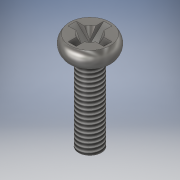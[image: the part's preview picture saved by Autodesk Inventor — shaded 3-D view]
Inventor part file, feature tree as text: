
AUTODESK INVENTOR PART (.ipt)
format: ipt  version: 2019 (Build 230136000, 136)  size: 164,864 bytes
history: native  units: mm
features: sketch x2, revolve x1, extrude x1, pattern_circular x1, thread x1
ambient origin geometry x8: Origin, YZ Plane, XZ Plane, XY Plane, X Axis, Y Axis, Z Axis, Center Point
bodies: Body1 (feature_tree)
feature tree (6):
  revolve  "Вращение1"
  extrude  "Выдавливание2"  Depth=2.8mm
  pattern_circular  "Круговой массив1"  [2 undecoded]
  thread  "Резьба1"
  sketch  "Эскиз3"
  sketch  "Эскиз5"
note: 2 required parameter values undecoded (feature->parameter linkage not recoverable at this tier; creation-order binding heuristic only, values carry confidence <= 0.55)
